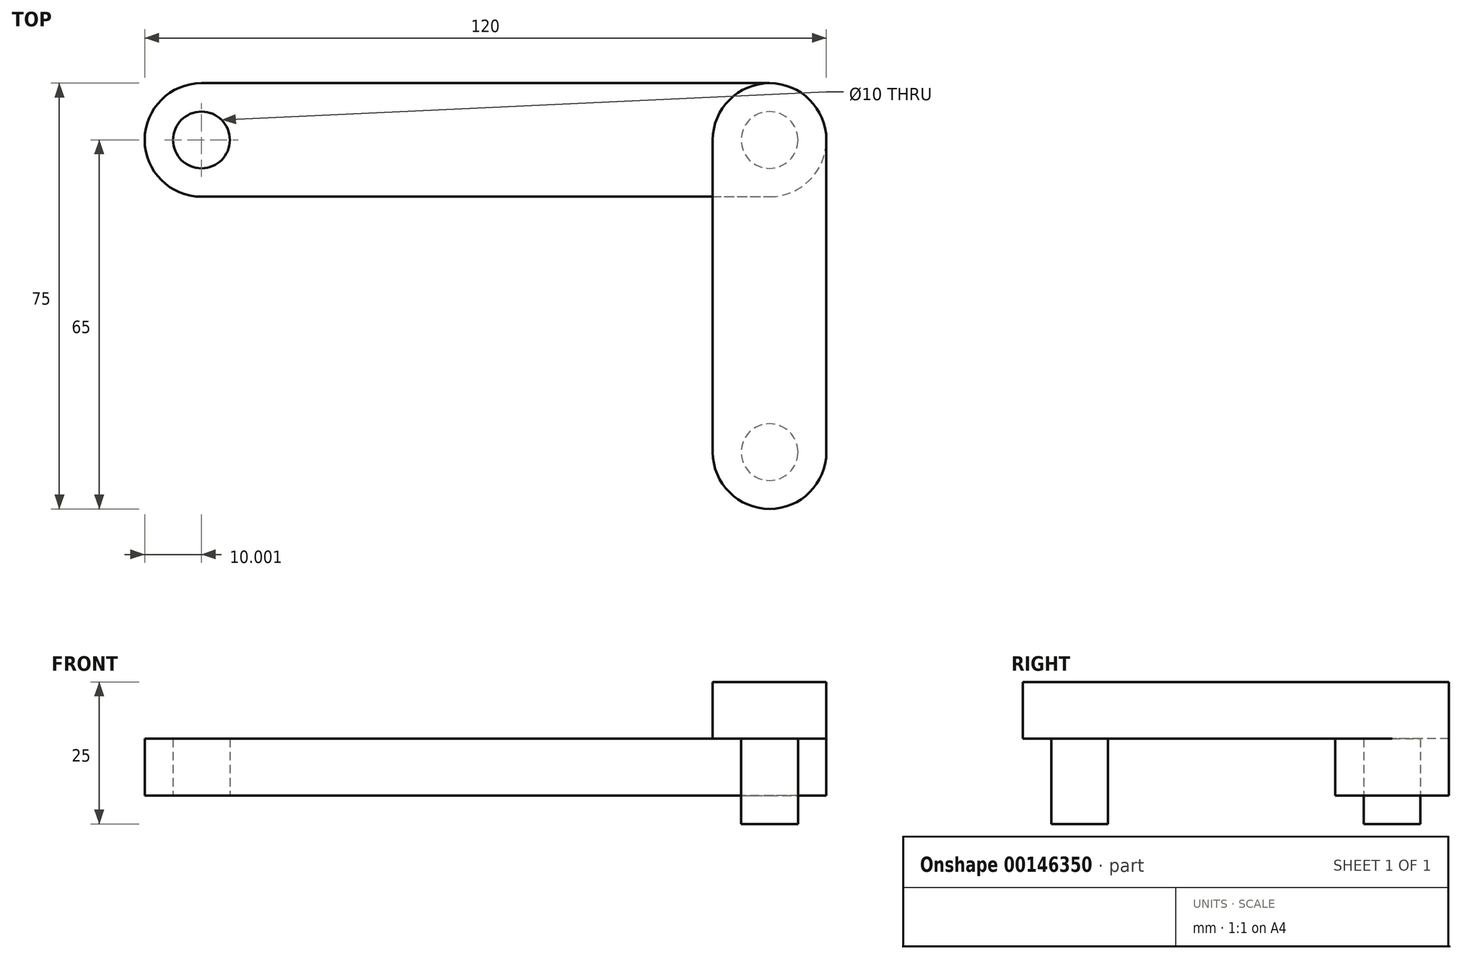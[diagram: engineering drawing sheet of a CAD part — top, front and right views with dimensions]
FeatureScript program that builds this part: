
annotation { "Feature Type Name" : "Feature", "Feature Type Description" : "" }
export const myFeature = defineFeature(function(context is Context, id is Id, definition is map)
    precondition{}
    {
        {
            var Q0;
            Q0=qCreatedBy(makeId("Top.planeOp"),FACE);
            var sketch = newSketch(context, id + "F0", { "sketchPlane" : qUnion([Q0])});
            skLineSegment(sketch, "E0.bottom", {"start": v(-88.92, 0) * mm, "end": v(11.08, 0) * mm});
            skLineSegment(sketch, "E0.top", {"start": v(-88.92, -20) * mm, "end": v(11.08, -20) * mm});
            skArc(sketch, "E1", {"start": v(-88.92, 0) * mm, "mid": v(-98.92, -10) * mm, "end": v(-88.92, -20) * mm});
            skArc(sketch, "E2", {"start": v(11.08, -20) * mm, "mid": v(21.08, -10) * mm, "end": v(11.08, 0) * mm});
            skCircle(sketch, "E3", {"center": v(11.08, -10) * mm, "radius": 5 * mm});
            skCircle(sketch, "E4", {"center": v(-88.92, -10) * mm, "radius": 5 * mm});
            skSolve(sketch);
        }
        {
            var Q0;
            Q0 = qSketchRegion(id + "F0", true);
            extrude(context, id + "F1", {"entities" : qUnion([Q0]), "depth" : 10 * mm});
        }
        {
            var Q0;
            Q0=makeQuery(id+"F1.opExtrude","CAP_FACE",FACE,{"disambiguationData":[OSD([sQuery(id+"F0.wireOp",EDGE,"E0.bottom"),sQuery(id+"F0.wireOp",EDGE,"E0.top"),sQuery(id+"F0.wireOp",EDGE,"E1"),sQuery(id+"F0.wireOp",EDGE,"E2"),sQuery(id+"F0.wireOp",EDGE,"E3"),sQuery(id+"F0.wireOp",EDGE,"E4")])],"isStart":false});
            var sketch = newSketch(context, id + "F2", { "sketchPlane" : qUnion([Q0])});
            skCircle(sketch, "E5", {"center": v(11.08, -10) * mm, "radius": 10 * mm});
            skPoint(sketch, "E6.oppositeSnap0", {"position": v(21.08, -10) * mm});
            skLineSegment(sketch, "E6.bottom", {"start": v(1.08, -10) * mm, "end": v(21.08, -10) * mm});
            skLineSegment(sketch, "E6.top", {"start": v(6.08, -65) * mm, "end": v(16.08, -65) * mm});
            skLineSegment(sketch, "E6.left", {"start": v(1.08, -10) * mm, "end": v(1.08, -65) * mm});
            skLineSegment(sketch, "E6.right", {"start": v(21.08, -10) * mm, "end": v(21.08, -65) * mm});
            skCircle(sketch, "E7", {"center": v(11.08, -65) * mm, "radius": 10 * mm});
            skCircle(sketch, "E8", {"center": v(11.08, -65) * mm, "radius": 5 * mm});
            skSolve(sketch);
        }
        {
            var Q0;
            {var subQ4=sQuery(id+"F2.wireOp",EDGE,"E6.right");Q0=makeQuery(id+"F2.imprint","IMPRINT",FACE,{"disambiguationData":[TD([[makeQuery(id+"F2.imprint","IMPRINT",EDGE,{"derivedFrom":subQ4}),-1.0]])]});}
            var Q1;
            {var subQ0=sQuery(id+"F2.wireOp",EDGE,"E6.bottom");var subQ3=makeQuery(id+"F1.opExtrude","CAP_EDGE",EDGE,{"disambiguationData":[OSD([sQuery(id+"F0.wireOp",EDGE,"E3")])],"isStart":false});var subQ4=makeQuery(id+"F2.imprint","INTERSECT",VERTEX,{"disambiguationData":[OD(0.0)],"derivedFrom":[subQ3,subQ0]});Q1=makeQuery(id+"F2.imprint","IMPRINT",FACE,{"disambiguationData":[TD([[makeQuery(id+"F2.imprint","IMPRINT",EDGE,{"disambiguationData":[TD([[subQ4,-1.0]])],"derivedFrom":subQ3}),-1.0]])]});}
            var Q2;
            {var subQ0=sQuery(id+"F2.wireOp",EDGE,"E5");var subQ1=makeQuery(id+"F1.opExtrude","CAP_EDGE",EDGE,{"disambiguationData":[OSD([sQuery(id+"F0.wireOp",EDGE,"E0.top")])],"isStart":false});var subQ2=makeQuery(id+"F2.imprint","INTERSECT",VERTEX,{"derivedFrom":[subQ1,subQ0]});Q2=makeQuery(id+"F2.imprint","IMPRINT",FACE,{"disambiguationData":[TD([[makeQuery(id+"F2.imprint","IMPRINT",EDGE,{"disambiguationData":[TD([[subQ2,1.0]])],"derivedFrom":subQ1}),1.0]])]});}
            var Q3;
            {var subQ0=sQuery(id+"F2.wireOp",EDGE,"E6.bottom");var subQ3=makeQuery(id+"F1.opExtrude","CAP_EDGE",EDGE,{"disambiguationData":[OSD([sQuery(id+"F0.wireOp",EDGE,"E3")])],"isStart":false});var subQ4=makeQuery(id+"F2.imprint","INTERSECT",VERTEX,{"disambiguationData":[OD(0.0)],"derivedFrom":[subQ3,subQ0]});Q3=makeQuery(id+"F2.imprint","IMPRINT",FACE,{"disambiguationData":[TD([[makeQuery(id+"F2.imprint","IMPRINT",EDGE,{"disambiguationData":[TD([[subQ4,1.0]])],"derivedFrom":subQ3}),-1.0]])]});}
            var Q4;
            {var subQ1=sQuery(id+"F2.wireOp",EDGE,"E6.top");var subQ3=sQuery(id+"F2.wireOp",EDGE,"E8");var subQ4=makeQuery(id+"F2.imprint","INTERSECT",VERTEX,{"disambiguationData":[OD(0.0)],"derivedFrom":[subQ1,subQ3]});Q4=makeQuery(id+"F2.imprint","IMPRINT",FACE,{"disambiguationData":[TD([[makeQuery(id+"F2.imprint","IMPRINT",EDGE,{"disambiguationData":[TD([[subQ4,-1.0]])],"derivedFrom":subQ3}),-1.0]])]});}
            var Q5;
            {var subQ1=sQuery(id+"F2.wireOp",EDGE,"E6.top");var subQ3=sQuery(id+"F2.wireOp",EDGE,"E8");var subQ4=makeQuery(id+"F2.imprint","INTERSECT",VERTEX,{"disambiguationData":[OD(0.0)],"derivedFrom":[subQ1,subQ3]});Q5=makeQuery(id+"F2.imprint","IMPRINT",FACE,{"disambiguationData":[TD([[makeQuery(id+"F2.imprint","IMPRINT",EDGE,{"disambiguationData":[TD([[subQ4,1.0]])],"derivedFrom":subQ3}),-1.0]])]});}
            var Q6;
            {var subQ0=sQuery(id+"F2.wireOp",EDGE,"E6.bottom");var subQ1=makeQuery(id+"F1.opExtrude","CAP_EDGE",EDGE,{"disambiguationData":[OSD([sQuery(id+"F0.wireOp",EDGE,"E3")])],"isStart":false});var subQ2=makeQuery(id+"F2.imprint","INTERSECT",VERTEX,{"disambiguationData":[OD(0.0)],"derivedFrom":[subQ1,subQ0]});Q6=makeQuery(id+"F2.imprint","IMPRINT",FACE,{"disambiguationData":[TD([[makeQuery(id+"F2.imprint","IMPRINT",EDGE,{"disambiguationData":[TD([[subQ2,-1.0]])],"derivedFrom":subQ0}),-1.0]])]});}
            var Q7;
            {var subQ0=sQuery(id+"F2.wireOp",EDGE,"E6.bottom");var subQ1=makeQuery(id+"F1.opExtrude","CAP_EDGE",EDGE,{"disambiguationData":[OSD([sQuery(id+"F0.wireOp",EDGE,"E3")])],"isStart":false});var subQ2=makeQuery(id+"F2.imprint","INTERSECT",VERTEX,{"disambiguationData":[OD(0.0)],"derivedFrom":[subQ1,subQ0]});Q7=makeQuery(id+"F2.imprint","IMPRINT",FACE,{"disambiguationData":[TD([[makeQuery(id+"F2.imprint","IMPRINT",EDGE,{"disambiguationData":[TD([[subQ2,-1.0]])],"derivedFrom":subQ0}),1.0]])]});}
            var Q8;
            {var subQ0=sQuery(id+"F2.wireOp",EDGE,"E8");var subQ1=sQuery(id+"F2.wireOp",EDGE,"E6.top");var subQ2=makeQuery(id+"F2.imprint","INTERSECT",VERTEX,{"disambiguationData":[OD(0.0)],"derivedFrom":[subQ1,subQ0]});Q8=makeQuery(id+"F2.imprint","IMPRINT",FACE,{"disambiguationData":[TD([[makeQuery(id+"F2.imprint","IMPRINT",EDGE,{"disambiguationData":[TD([[subQ2,-1.0]])],"derivedFrom":subQ1}),1.0]])]});}
            var Q9;
            {var subQ0=sQuery(id+"F2.wireOp",EDGE,"E8");var subQ1=sQuery(id+"F2.wireOp",EDGE,"E6.top");var subQ2=makeQuery(id+"F2.imprint","INTERSECT",VERTEX,{"disambiguationData":[OD(0.0)],"derivedFrom":[subQ1,subQ0]});Q9=makeQuery(id+"F2.imprint","IMPRINT",FACE,{"disambiguationData":[TD([[makeQuery(id+"F2.imprint","IMPRINT",EDGE,{"disambiguationData":[TD([[subQ2,-1.0]])],"derivedFrom":subQ1}),-1.0]])]});}
            extrude(context, id + "F3", {"entities" : qUnion([Q0, Q1, Q2, Q3, Q4, Q5, Q6, Q7, Q8, Q9]), "depth" : 10 * mm});
        }
        {
            var Q0;
            {var subQ0=sQuery(id+"F2.wireOp",EDGE,"E6.bottom");var subQ1=makeQuery(id+"F1.opExtrude","CAP_EDGE",EDGE,{"disambiguationData":[OSD([sQuery(id+"F0.wireOp",EDGE,"E3")])],"isStart":false});var subQ2=makeQuery(id+"F2.imprint","INTERSECT",VERTEX,{"disambiguationData":[OD(0.0)],"derivedFrom":[subQ1,subQ0]});Q0=makeQuery(id+"F2.imprint","IMPRINT",FACE,{"disambiguationData":[TD([[makeQuery(id+"F2.imprint","IMPRINT",EDGE,{"disambiguationData":[TD([[subQ2,-1.0]])],"derivedFrom":subQ0}),1.0]])]});}
            var Q1;
            {var subQ0=sQuery(id+"F2.wireOp",EDGE,"E6.bottom");var subQ1=makeQuery(id+"F1.opExtrude","CAP_EDGE",EDGE,{"disambiguationData":[OSD([sQuery(id+"F0.wireOp",EDGE,"E3")])],"isStart":false});var subQ2=makeQuery(id+"F2.imprint","INTERSECT",VERTEX,{"disambiguationData":[OD(0.0)],"derivedFrom":[subQ1,subQ0]});Q1=makeQuery(id+"F2.imprint","IMPRINT",FACE,{"disambiguationData":[TD([[makeQuery(id+"F2.imprint","IMPRINT",EDGE,{"disambiguationData":[TD([[subQ2,-1.0]])],"derivedFrom":subQ0}),-1.0]])]});}
            extrude(context, id + "F4", {"entities" : qUnion([Q0, Q1]), "operationType" : NewBodyOperationType.ADD, "oppositeDirection" : true, "depth" : 15 * mm});
        }
        {
            var Q0;
            {var subQ0=sQuery(id+"F2.wireOp",EDGE,"E8");var subQ1=sQuery(id+"F2.wireOp",EDGE,"E6.top");var subQ2=makeQuery(id+"F2.imprint","INTERSECT",VERTEX,{"disambiguationData":[OD(0.0)],"derivedFrom":[subQ1,subQ0]});Q0=makeQuery(id+"F2.imprint","IMPRINT",FACE,{"disambiguationData":[TD([[makeQuery(id+"F2.imprint","IMPRINT",EDGE,{"disambiguationData":[TD([[subQ2,-1.0]])],"derivedFrom":subQ1}),-1.0]])]});}
            var Q1;
            {var subQ0=sQuery(id+"F2.wireOp",EDGE,"E8");var subQ1=sQuery(id+"F2.wireOp",EDGE,"E6.top");var subQ2=makeQuery(id+"F2.imprint","INTERSECT",VERTEX,{"disambiguationData":[OD(0.0)],"derivedFrom":[subQ1,subQ0]});Q1=makeQuery(id+"F2.imprint","IMPRINT",FACE,{"disambiguationData":[TD([[makeQuery(id+"F2.imprint","IMPRINT",EDGE,{"disambiguationData":[TD([[subQ2,-1.0]])],"derivedFrom":subQ1}),1.0]])]});}
            extrude(context, id + "F5", {"entities" : qUnion([Q0, Q1]), "operationType" : NewBodyOperationType.ADD, "oppositeDirection" : true, "depth" : 15 * mm});
        }
    });
